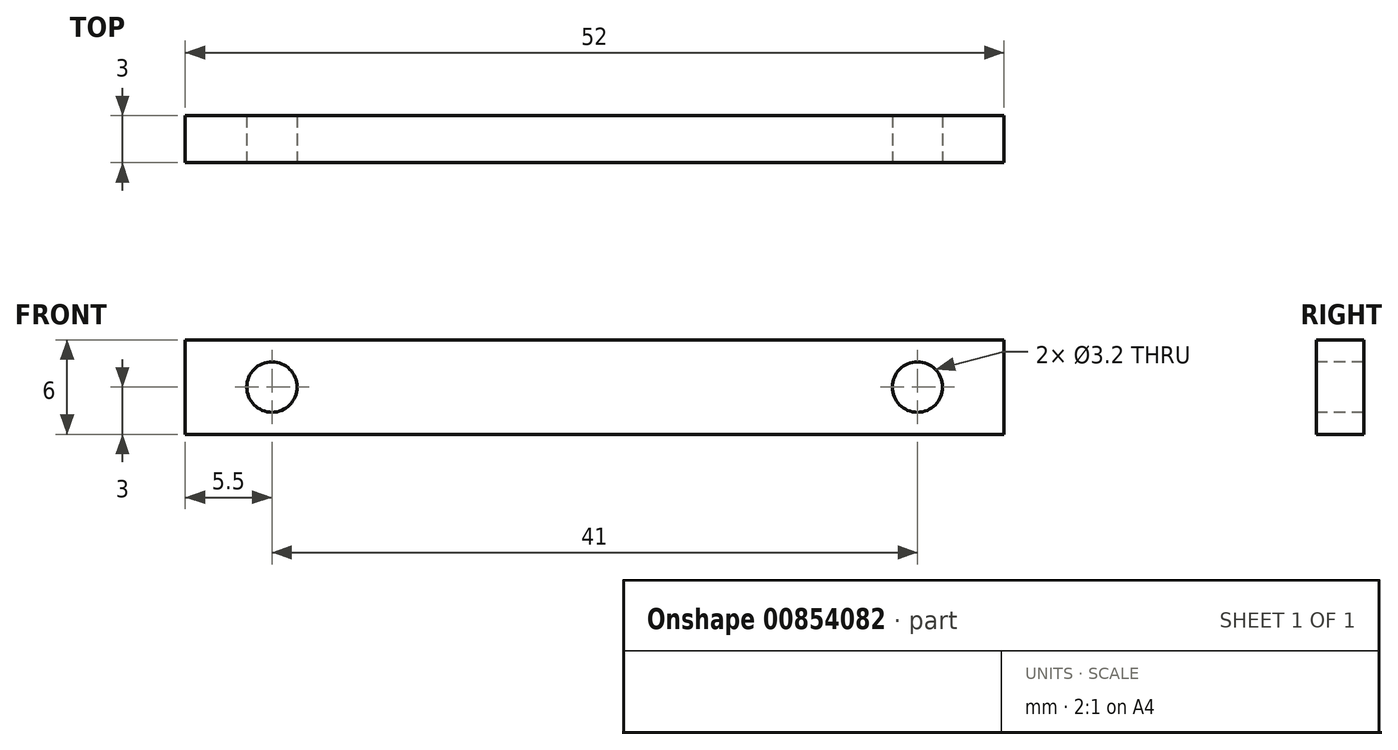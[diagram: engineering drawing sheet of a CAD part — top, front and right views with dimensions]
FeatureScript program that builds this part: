
annotation { "Feature Type Name" : "Feature", "Feature Type Description" : "" }
export const myFeature = defineFeature(function(context is Context, id is Id, definition is map)
    precondition{}
    {
        {
            var Q0;
            Q0=qCreatedBy(makeId("Front.planeOp"),FACE);
            var sketch = newSketch(context, id + "F0", { "sketchPlane" : qUnion([Q0])});
            skLineSegment(sketch, "E0.bottom", {"start": v(0, 0) * mm, "end": v(52, 0) * mm});
            skLineSegment(sketch, "E0.top", {"start": v(0, 6) * mm, "end": v(52, 6) * mm});
            skLineSegment(sketch, "E0.left", {"start": v(0, 0) * mm, "end": v(0, 6) * mm});
            skLineSegment(sketch, "E0.right", {"start": v(52, 0) * mm, "end": v(52, 6) * mm});
            skSolve(sketch);
        }
        {
            var Q0;
            Q0 = qSketchRegion(id + "F0", true);
            extrude(context, id + "F1", {"entities" : qUnion([Q0]), "depth" : 3 * mm, "offsetDistance" : 25 * mm});
        }
        {
            var Q0;
            Q0=qCreatedBy(makeId("Front.planeOp"),FACE);
            var sketch = newSketch(context, id + "F2", { "sketchPlane" : qUnion([Q0])});
            skPoint(sketch, "E1", {"position": v(5.5, 3) * mm});
            skPoint(sketch, "E2", {"position": v(46.5, 3) * mm});
            skSolve(sketch);
        }
        {
            var Q0;
            Q0=sQuery(id+"F2.wireOp",VERTEX,"E1");
            var Q1;
            Q1=sQuery(id+"F2.wireOp",VERTEX,"E2");
            var Q2;
            Q2=makeQuery(id+"F1.opExtrude","SWEPT_BODY",BODY,{"disambiguationData":[OSD([sQuery(id+"F0.wireOp",EDGE,"E0.bottom"),sQuery(id+"F0.wireOp",EDGE,"E0.top"),sQuery(id+"F0.wireOp",EDGE,"E0.left"),sQuery(id+"F0.wireOp",EDGE,"E0.right")])]});
            hole(context, id + "F3", {"style" : HoleStyle.SIMPLE, "endStyle" : HoleEndStyle.THROUGH, "oppositeDirection" : true, "holeDiameter" : 3.2 * mm, "majorDiameter" : 5 * mm, "isTappedThrough" : true, "tappedDepth" : 12 * mm, "tapClearance" : 3, "locations" : qUnion([Q0, Q1]), "scope" : qUnion([Q2]), "startStyle" : HoleStartStyle.SKETCH});
        }
    });
